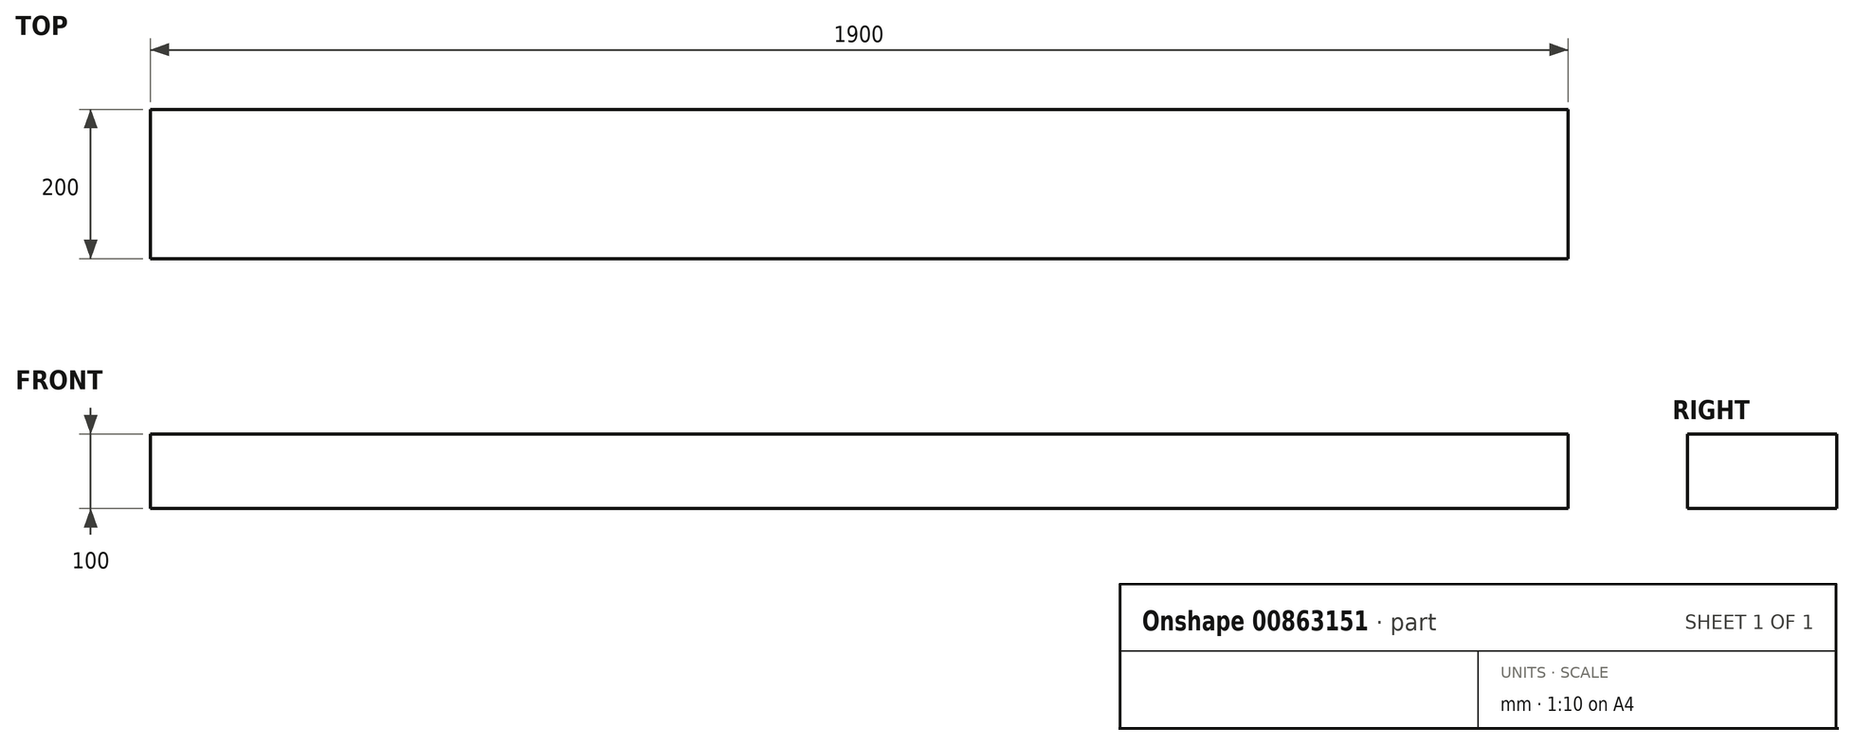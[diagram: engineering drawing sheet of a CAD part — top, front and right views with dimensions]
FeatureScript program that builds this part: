
annotation { "Feature Type Name" : "Feature", "Feature Type Description" : "" }
export const myFeature = defineFeature(function(context is Context, id is Id, definition is map)
    precondition{}
    {
        {
            var Q0;
            Q0=qCreatedBy(makeId("Top.planeOp"),FACE);
            var sketch = newSketch(context, id + "F0", { "sketchPlane" : qUnion([Q0])});
            skLineSegment(sketch, "E0", {"start": v(0, 0) * mm, "end": v(0, 200) * mm});
            skLineSegment(sketch, "E1", {"start": v(0, 200) * mm, "end": v(1900, 200) * mm});
            skLineSegment(sketch, "E2", {"start": v(1900, 200) * mm, "end": v(1900, 0) * mm});
            skLineSegment(sketch, "E3", {"start": v(1900, 0) * mm, "end": v(0, 0) * mm});
            skSolve(sketch);
        }
        {
            var Q0;
            Q0=makeQuery(id+"F0.imprint","IMPRINT",FACE,{"disambiguationData":[TD([[makeQuery(id+"F0.imprint","IMPRINT",EDGE,{"derivedFrom":sQuery(id+"F0.wireOp",EDGE,"E0")}),-1.0]])]});
            extrude(context, id + "F1", {"entities" : qUnion([Q0]), "depth" : 100 * mm, "offsetDistance" : 25 * mm});
        }
    });
